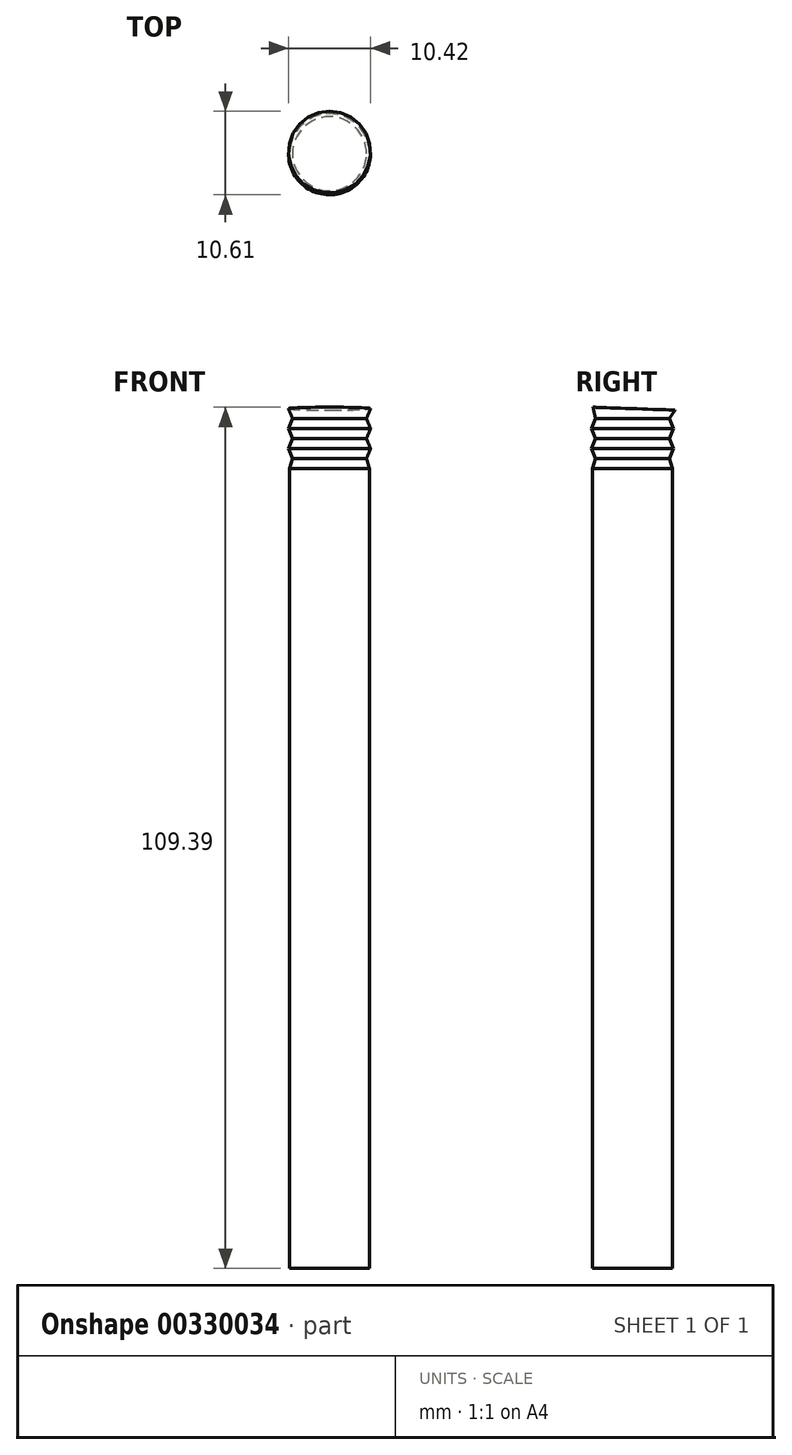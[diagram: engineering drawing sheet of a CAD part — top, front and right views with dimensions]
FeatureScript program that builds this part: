
annotation { "Feature Type Name" : "Feature", "Feature Type Description" : "" }
export const myFeature = defineFeature(function(context is Context, id is Id, definition is map)
    precondition{}
    {
        {
            var Q0;
            Q0=qCreatedBy(makeId("Top.planeOp"),FACE);
            var sketch = newSketch(context, id + "F0", { "sketchPlane" : qUnion([Q0])});
            skCircle(sketch, "E0", {"center": v(0, 0) * mm, "radius": 5.08 * mm});
            skSolve(sketch);
        }
        {
            var Q0;
            Q0=qCreatedBy(makeId("Top.planeOp"),FACE);
            cPlane(context, id + "F1", {"entities" : qUnion([Q0]), "cplaneType" : CPlaneType.OFFSET, "offset" : 101.6 * mm, "width" : 152.4 * mm, "height" : 152.4 * mm});
        }
        {
            var Q0;
            Q0=qCreatedBy(id+"F1.planeOp",FACE);
            var sketch = newSketch(context, id + "F2", { "sketchPlane" : qUnion([Q0])});
            skCircle(sketch, "E1", {"center": v(0, 0) * mm, "radius": 5.08 * mm});
            skSolve(sketch);
        }
        {
            var Q0;
            Q0=makeQuery(id+"F0.imprint","IMPRINT",FACE,{"disambiguationData":[TD([[makeQuery(id+"F0.imprint","IMPRINT",EDGE,{"derivedFrom":sQuery(id+"F0.wireOp",EDGE,"E0")}),1.0]])]});
            var Q1;
            Q1=makeQuery(id+"F2.imprint","IMPRINT",FACE,{"disambiguationData":[TD([[makeQuery(id+"F2.imprint","IMPRINT",EDGE,{"derivedFrom":sQuery(id+"F2.wireOp",EDGE,"E1")}),1.0]])]});
            loft(context, id + "F3", {"sheetProfilesArray" : [{ "sheetProfileEntities" : qUnion([Q0]) }, { "sheetProfileEntities" : qUnion([Q1]) }]});
        }
        {
            var Q0;
            Q0=qCreatedBy(id+"F1.planeOp",FACE);
            cPlane(context, id + "F4", {"entities" : qUnion([Q0]), "cplaneType" : CPlaneType.OFFSET, "offset" : 1.27 * mm, "width" : 152.4 * mm, "height" : 152.4 * mm});
        }
        {
            var Q0;
            Q0=qCreatedBy(id+"F4.planeOp",FACE);
            var sketch = newSketch(context, id + "F5", { "sketchPlane" : qUnion([Q0])});
            skCircle(sketch, "E2", {"center": v(0, 0) * mm, "radius": 4.7 * mm});
            skSolve(sketch);
        }
        {
            var Q1;
            Q1=makeQuery(id+"F3.opLoft","CAP_FACE",FACE,{"disambiguationData":[OSD([makeQuery(id+"F2.imprint","IMPRINT",FACE,{"disambiguationData":[TD([[makeQuery(id+"F2.imprint","IMPRINT",EDGE,{"derivedFrom":sQuery(id+"F2.wireOp",EDGE,"E1")}),1.0]])]})])],"isStart":true});
            var Q2;
            Q2=makeQuery(id+"F5.imprint","IMPRINT",FACE,{"disambiguationData":[TD([[makeQuery(id+"F5.imprint","IMPRINT",EDGE,{"derivedFrom":sQuery(id+"F5.wireOp",EDGE,"E2")}),1.0]])]});
            loft(context, id + "F6", {"operationType" : NewBodyOperationType.ADD, "sheetProfilesArray" : [{ "sheetProfileEntities" : qUnion([Q1]) }, { "sheetProfileEntities" : qUnion([Q2]) }]});
        }
        {
            var Q0;
            Q0=qCreatedBy(id+"F4.planeOp",FACE);
            cPlane(context, id + "F7", {"entities" : qUnion([Q0]), "cplaneType" : CPlaneType.OFFSET, "offset" : 1.27 * mm, "width" : 152.4 * mm, "height" : 152.4 * mm});
        }
        {
            var Q0;
            Q0=qCreatedBy(id+"F7.planeOp",FACE);
            var sketch = newSketch(context, id + "F8", { "sketchPlane" : qUnion([Q0])});
            skCircle(sketch, "E3", {"center": v(0, 0) * mm, "radius": 5.2 * mm});
            skSolve(sketch);
        }
        {
            var Q1;
            Q1=makeQuery(id+"F8.imprint","IMPRINT",FACE,{"disambiguationData":[TD([[makeQuery(id+"F8.imprint","IMPRINT",EDGE,{"derivedFrom":sQuery(id+"F8.wireOp",EDGE,"E3")}),1.0]])]});
            var Q2;
            Q2=makeQuery(id+"F5.imprint","IMPRINT",FACE,{"disambiguationData":[TD([[makeQuery(id+"F5.imprint","IMPRINT",EDGE,{"derivedFrom":sQuery(id+"F5.wireOp",EDGE,"E2")}),1.0]])]});
            loft(context, id + "F9", {"operationType" : NewBodyOperationType.ADD, "sheetProfilesArray" : [{ "sheetProfileEntities" : qUnion([Q1]) }, { "sheetProfileEntities" : qUnion([Q2]) }]});
        }
        {
            var Q0;
            Q0=qCreatedBy(id+"F7.planeOp",FACE);
            cPlane(context, id + "F10", {"entities" : qUnion([Q0]), "cplaneType" : CPlaneType.OFFSET, "offset" : 1.27 * mm, "width" : 152.4 * mm, "height" : 152.4 * mm});
        }
        {
            var Q0;
            Q0=qCreatedBy(id+"F10.planeOp",FACE);
            var sketch = newSketch(context, id + "F11", { "sketchPlane" : qUnion([Q0])});
            skCircle(sketch, "E4", {"center": v(0, 0) * mm, "radius": 4.7 * mm});
            skSolve(sketch);
        }
        {
            var Q1;
            Q1=makeQuery(id+"F8.imprint","IMPRINT",FACE,{"disambiguationData":[TD([[makeQuery(id+"F8.imprint","IMPRINT",EDGE,{"derivedFrom":sQuery(id+"F8.wireOp",EDGE,"E3")}),1.0]])]});
            var Q2;
            Q2=makeQuery(id+"F11.imprint","IMPRINT",FACE,{"disambiguationData":[TD([[makeQuery(id+"F11.imprint","IMPRINT",EDGE,{"derivedFrom":sQuery(id+"F11.wireOp",EDGE,"E4")}),1.0]])]});
            loft(context, id + "F12", {"operationType" : NewBodyOperationType.ADD, "sheetProfilesArray" : [{ "sheetProfileEntities" : qUnion([Q1]) }, { "sheetProfileEntities" : qUnion([Q2]) }]});
        }
        {
            var Q0;
            Q0=qCreatedBy(id+"F10.planeOp",FACE);
            cPlane(context, id + "F13", {"entities" : qUnion([Q0]), "cplaneType" : CPlaneType.OFFSET, "offset" : 1.27 * mm, "width" : 152.4 * mm, "height" : 152.4 * mm});
        }
        {
            var Q0;
            Q0=qCreatedBy(id+"F13.planeOp",FACE);
            var sketch = newSketch(context, id + "F14", { "sketchPlane" : qUnion([Q0])});
            skCircle(sketch, "E5", {"center": v(0, 0) * mm, "radius": 5.2 * mm});
            skSolve(sketch);
        }
        {
            var Q1;
            Q1=makeQuery(id+"F14.imprint","IMPRINT",FACE,{"disambiguationData":[TD([[makeQuery(id+"F14.imprint","IMPRINT",EDGE,{"derivedFrom":sQuery(id+"F14.wireOp",EDGE,"E5")}),1.0]])]});
            var Q2;
            Q2=makeQuery(id+"F11.imprint","IMPRINT",FACE,{"disambiguationData":[TD([[makeQuery(id+"F11.imprint","IMPRINT",EDGE,{"derivedFrom":sQuery(id+"F11.wireOp",EDGE,"E4")}),1.0]])]});
            loft(context, id + "F15", {"operationType" : NewBodyOperationType.ADD, "sheetProfilesArray" : [{ "sheetProfileEntities" : qUnion([Q1]) }, { "sheetProfileEntities" : qUnion([Q2]) }]});
        }
        {
            var Q0;
            Q0=qCreatedBy(id+"F10.planeOp",FACE);
            cPlane(context, id + "F16", {"entities" : qUnion([Q0]), "cplaneType" : CPlaneType.OFFSET, "offset" : 1.27 * mm, "width" : 152.4 * mm, "height" : 152.4 * mm});
        }
        {
            var Q0;
            Q0=qCreatedBy(id+"F16.planeOp",FACE);
            cPlane(context, id + "F17", {"entities" : qUnion([Q0]), "cplaneType" : CPlaneType.OFFSET, "offset" : 1.27 * mm, "width" : 152.4 * mm, "height" : 152.4 * mm});
        }
        {
            var Q0;
            Q0=qCreatedBy(id+"F17.planeOp",FACE);
            var sketch = newSketch(context, id + "F18", { "sketchPlane" : qUnion([Q0])});
            skCircle(sketch, "E6", {"center": v(0, 0) * mm, "radius": 4.7 * mm});
            skSolve(sketch);
        }
        {
            var Q1;
            Q1=makeQuery(id+"F14.imprint","IMPRINT",FACE,{"disambiguationData":[TD([[makeQuery(id+"F14.imprint","IMPRINT",EDGE,{"derivedFrom":sQuery(id+"F14.wireOp",EDGE,"E5")}),1.0]])]});
            var Q2;
            Q2=makeQuery(id+"F18.imprint","IMPRINT",FACE,{"disambiguationData":[TD([[makeQuery(id+"F18.imprint","IMPRINT",EDGE,{"derivedFrom":sQuery(id+"F18.wireOp",EDGE,"E6")}),1.0]])]});
            loft(context, id + "F19", {"operationType" : NewBodyOperationType.ADD, "sheetProfilesArray" : [{ "sheetProfileEntities" : qUnion([Q1]) }, { "sheetProfileEntities" : qUnion([Q2]) }]});
        }
        {
            var Q0;
            Q0=qCreatedBy(id+"F17.planeOp",FACE);
            cPlane(context, id + "F20", {"entities" : qUnion([Q0]), "cplaneType" : CPlaneType.OFFSET, "offset" : 1.27 * mm, "width" : 152.4 * mm, "height" : 152.4 * mm});
        }
        {
            var Q0;
            Q0=qCreatedBy(id+"F20.planeOp",FACE);
            var sketch = newSketch(context, id + "F21", { "sketchPlane" : qUnion([Q0])});
            skLineSegment(sketch, "E7", {"start": v(78.62, 0) * mm, "end": v(-76.58, 0) * mm, "construction": true});
            skSolve(sketch);
        }
        {
            var Q0;
            Q0=qCreatedBy(id+"F20.planeOp",FACE);
            var Q1;
            Q1=sQuery(id+"F21.wireOp",EDGE,"E7");
            cPlane(context, id + "F22", {"entities" : qUnion([Q0, Q1]), "cplaneType" : CPlaneType.LINE_ANGLE, "offset" : 25.4 * mm, "angle" : 2 * degree, "width" : 152.4 * mm, "height" : 152.4 * mm});
        }
        {
            var Q0;
            Q0=qCreatedBy(id+"F22.planeOp",FACE);
            var sketch = newSketch(context, id + "F23", { "sketchPlane" : qUnion([Q0])});
            skCircle(sketch, "E8", {"center": v(0, 3.61) * mm, "radius": 5.2 * mm});
            skSolve(sketch);
        }
        {
            var Q0;
            Q0=makeQuery(id+"F23.imprint","IMPRINT",FACE,{"disambiguationData":[TD([[makeQuery(id+"F23.imprint","IMPRINT",EDGE,{"derivedFrom":sQuery(id+"F23.wireOp",EDGE,"E8")}),1.0]])]});
            var Q1;
            Q1=makeQuery(id+"F18.imprint","IMPRINT",FACE,{"disambiguationData":[TD([[makeQuery(id+"F18.imprint","IMPRINT",EDGE,{"derivedFrom":sQuery(id+"F18.wireOp",EDGE,"E6")}),1.0]])]});
            loft(context, id + "F24", {"sheetProfilesArray" : [{ "sheetProfileEntities" : qUnion([Q0]) }, { "sheetProfileEntities" : qUnion([Q1]) }]});
        }
        {
            var Q0;
            Q0=qCreatedBy(id+"F22.planeOp",FACE);
            cPlane(context, id + "F25", {"entities" : qUnion([Q0]), "cplaneType" : CPlaneType.OFFSET, "offset" : 1.52 * mm, "oppositeDirection" : true, "width" : 152.4 * mm, "height" : 152.4 * mm});
        }
        {
            var Q0;
            Q0=qCreatedBy(id+"F25.planeOp",FACE);
            var sketch = newSketch(context, id + "F26", { "sketchPlane" : qUnion([Q0])});
            skLineSegment(sketch, "E9", {"start": v(89.93, 0) * mm, "end": v(-90.15, 0) * mm, "construction": true});
            skSolve(sketch);
        }
    });
